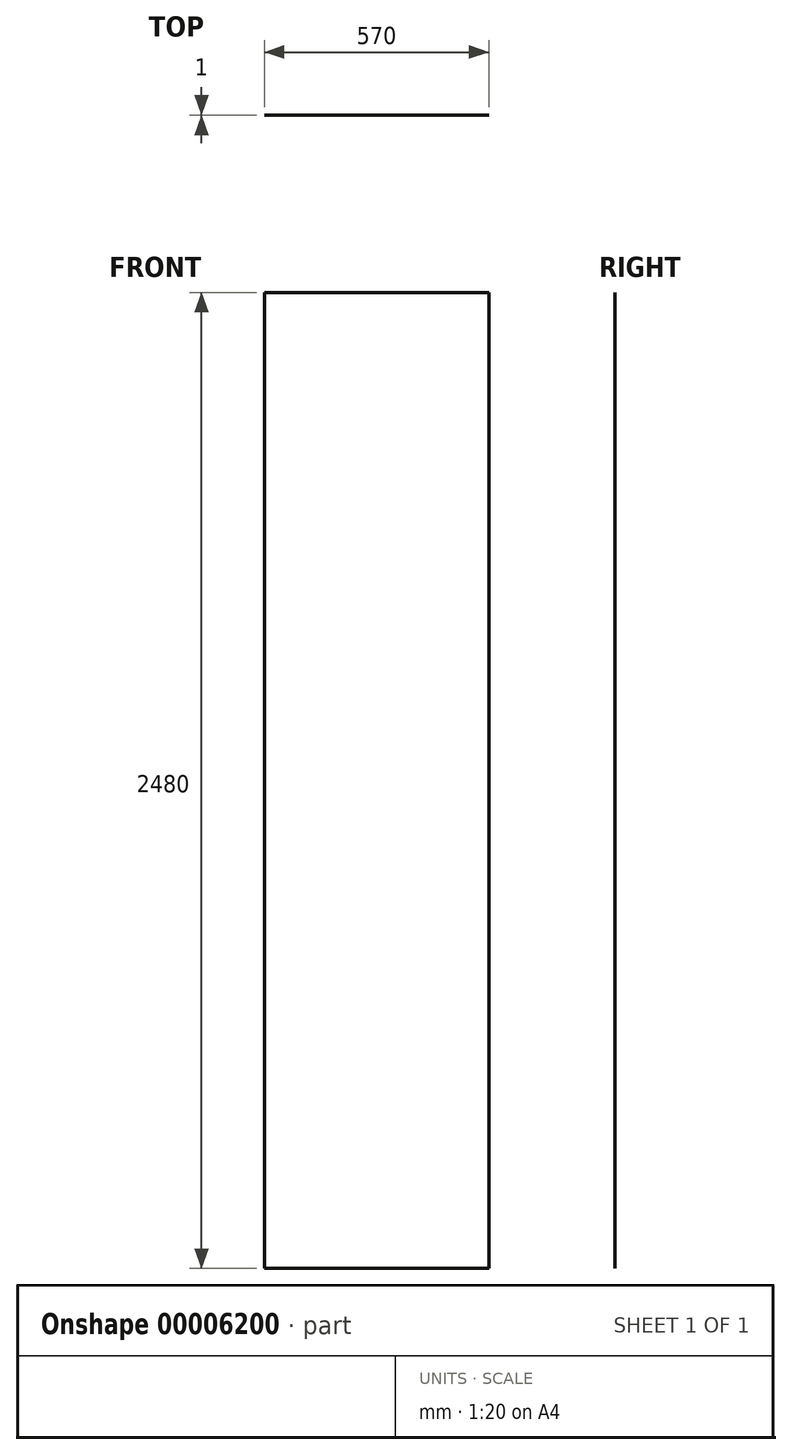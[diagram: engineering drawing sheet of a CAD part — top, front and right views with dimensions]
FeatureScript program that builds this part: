
annotation { "Feature Type Name" : "Feature", "Feature Type Description" : "" }
export const myFeature = defineFeature(function(context is Context, id is Id, definition is map)
    precondition{}
    {
        {
            var Q0;
            Q0=qCreatedBy(makeId("Front.planeOp"),FACE);
            var sketch = newSketch(context, id + "F0", { "sketchPlane" : qUnion([Q0])});
            skLineSegment(sketch, "E0.rect.bottom", {"start": v(285, -1240) * mm, "end": v(-285, -1240) * mm});
            skLineSegment(sketch, "E0.rect.top", {"start": v(285, 1240) * mm, "end": v(-285, 1240) * mm});
            skLineSegment(sketch, "E0.rect.left", {"start": v(285, -1240) * mm, "end": v(285, 1240) * mm});
            skLineSegment(sketch, "E0.rect.right", {"start": v(-285, -1240) * mm, "end": v(-285, 1240) * mm});
            skPoint(sketch, "E0.rect.middle", {"position": v(0, 0) * mm});
            skSolve(sketch);
        }
        {
            var Q0;
            Q0=makeQuery(id+"F0.imprint","IMPRINT",FACE,{"disambiguationData":[TD([[makeQuery(id+"F0.imprint","IMPRINT",EDGE,{"derivedFrom":sQuery(id+"F0.wireOp",EDGE,"E0.rect.bottom")}),-1.0]])]});
            extrude(context, id + "F1", {"entities" : qUnion([Q0]), "depth" : 1 * mm});
        }
    });
